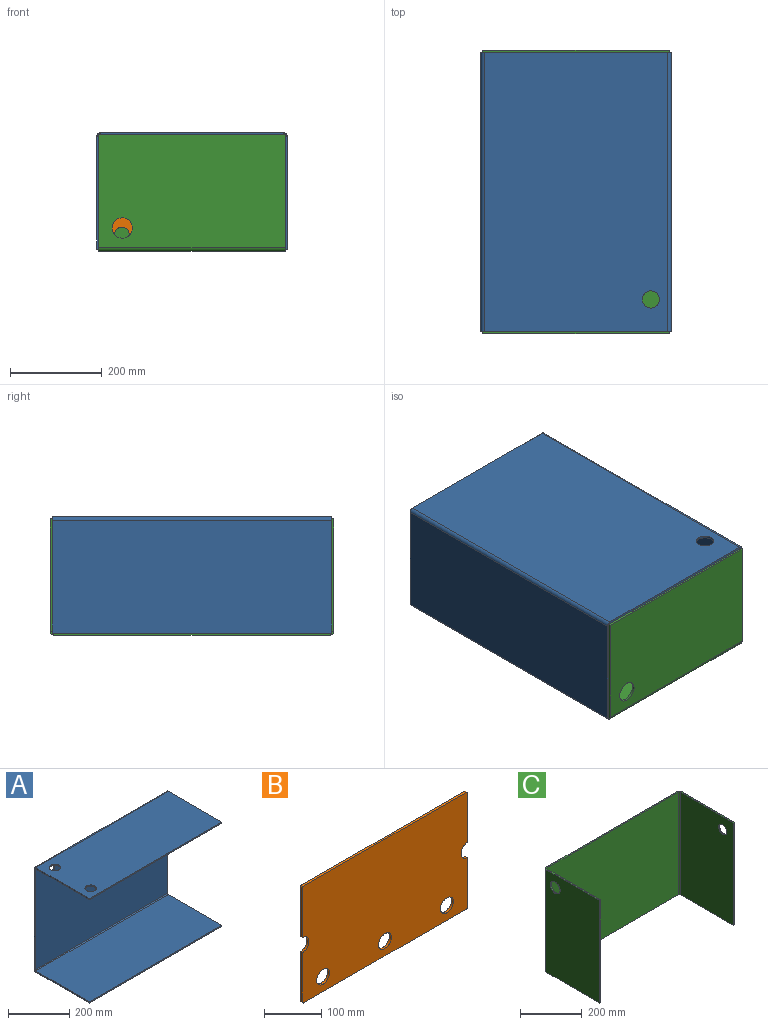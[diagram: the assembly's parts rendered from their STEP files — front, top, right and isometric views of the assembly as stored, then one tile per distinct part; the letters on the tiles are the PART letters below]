
ASSEMBLY  parts=3 mates=2
PART A: 25 faces, bbox 609.6x254x416 mm
  f0: plane 400.05x4.78mm, normal (-1,0,0), area 1910.3mm2, adj f3,f4,f13,f22
  f1: cylinder r=18.73mm len=37.47mm, axis (0,-1,0), area 562mm2, adj f3,f4
  f2: plane 400.05x4.78mm, normal (1,0,0), area 1910.3mm2, adj f3,f4,f12,f21
  f3: plane 609.6x400.05mm, normal (0,1,0), area 242768.1mm2, adj f0,f1,f2,f14,f23
  f4: plane 609.6x400.05mm, normal (0,-1,0), area 242768.1mm2, adj f0,f1,f2,f15,f24
  f5: plane 609.6x4.78mm, normal (0,-1,0), area 2911mm2, adj f6,f9,f10,f11
  f6: plane 246.05x4.78mm, normal (1,0,0), area 1174.9mm2, adj f5,f10,f11,f12
  f7: cylinder r=18.73mm len=37.47mm, axis (0,0,1), area 562mm2, adj f10,f11
  f8: cylinder r=18.73mm len=37.47mm, axis (0,0,1), area 562mm2, adj f10,f11
  f9: plane 246.05x4.78mm, normal (-1,0,0), area 1174.9mm2, adj f5,f10,f11,f13
  f10: plane 609.6x246.05mm, normal (0,0,1), area 147787.1mm2, adj f5,f6,f7,f8,f9,f14
  f11: plane 609.6x246.05mm, normal (0,0,-1), area 147787.1mm2, adj f5,f6,f7,f8,f9,f15
  f12: plane 7.95x7.95mm, normal (1,0,0), area 41.7mm2, adj f2,f6,f14,f15
  f13: plane 7.95x7.95mm, normal (-1,0,0), area 41.7mm2, adj f0,f9,f14,f15
  f14: cylinder r=7.95mm len=609.6mm, axis (1,0,0), area 7612.8mm2, adj f3,f10,f12,f13
  f15: cylinder r=3.17mm len=609.6mm, axis (1,0,0), area 3040.2mm2, adj f4,f11,f12,f13
  f16: plane 609.6x4.78mm, normal (0,-1,0), area 2911mm2, adj f17,f18,f19,f20
  f17: plane 246.05x4.78mm, normal (-1,0,0), area 1174.9mm2, adj f16,f19,f20,f22
  f18: plane 246.05x4.78mm, normal (1,0,0), area 1174.9mm2, adj f16,f19,f20,f21
  f19: plane 609.6x246.05mm, normal (0,0,-1), area 149992mm2, adj f16,f17,f18,f23
  f20: plane 609.6x246.05mm, normal (0,0,1), area 149992mm2, adj f16,f17,f18,f24
  f21: plane 7.95x7.95mm, normal (1,0,0), area 41.7mm2, adj f2,f18,f23,f24
  f22: plane 7.95x7.95mm, normal (-1,0,0), area 41.7mm2, adj f0,f17,f23,f24
  f23: cylinder r=7.95mm len=609.6mm, axis (1,0,0), area 7612.8mm2, adj f3,f19,f21,f22
  f24: cylinder r=3.17mm len=609.6mm, axis (1,0,0), area 3040.2mm2, adj f4,f20,f21,f22
PART B: 17 faces, bbox 406.4x4.8x248.9 mm
  f0: plane 400.05x4.78mm, normal (0,0,1), area 1910.3mm2, adj f1,f13,f15,f16
  f1: cylinder r=3.17mm len=4.78mm, axis (0,1,0), area 23.8mm2, adj f0,f2,f15,f16
  f2: plane 105.41x4.78mm, normal (-1,0,0), area 503.4mm2, adj f1,f3,f15,f16
  f3: cylinder r=15.88mm len=31.75mm, axis (0,1,0), area 238.2mm2, adj f2,f4,f15,f16
  f4: plane 105.41x4.78mm, normal (-1,0,0), area 503.4mm2, adj f3,f5,f15,f16
  f5: cylinder r=3.17mm len=4.78mm, axis (0,1,0), area 23.8mm2, adj f4,f6,f15,f16
  f6: plane 400.05x4.78mm, normal (0,0,-1), area 1910.3mm2, adj f5,f7,f15,f16
  f7: cylinder r=3.17mm len=4.78mm, axis (0,1,0), area 23.8mm2, adj f6,f8,f15,f16
  f8: plane 105.41x4.78mm, normal (1,0,0), area 503.4mm2, adj f7,f9,f15,f16
  f9: cylinder r=15.88mm len=31.75mm, axis (0,1,0), area 238.2mm2, adj f8,f10,f15,f16
  f10: plane 105.41x4.78mm, normal (1,0,0), area 503.4mm2, adj f9,f13,f15,f16
  f11: cylinder r=15.88mm len=31.75mm, axis (0,1,0), area 476.3mm2, adj f15,f16
  f12: cylinder r=15.88mm len=31.75mm, axis (0,1,0), area 476.3mm2, adj f15,f16
  f13: cylinder r=3.17mm len=4.78mm, axis (0,1,0), area 23.8mm2, adj f0,f10,f15,f16
  f14: cylinder r=15.88mm len=31.75mm, axis (0,1,0), area 476.3mm2, adj f15,f16
  f15: plane 406.4x248.92mm, normal (0,-1,0), area 97985.5mm2, adj f0,f1,f2,f3,f4,f5,f6,f7
  f16: plane 406.4x248.92mm, normal (0,1,0), area 97985.5mm2, adj f0,f1,f2,f3,f4,f5,f6,f7
PART C: 24 faces, bbox 619.2x254x406.4 mm
  f0: plane 603.25x4.78mm, normal (0,0,-1), area 2880.6mm2, adj f2,f3,f10,f20
  f1: plane 603.25x4.78mm, normal (0,0,1), area 2880.6mm2, adj f2,f3,f11,f21
  f2: plane 603.25x406.4mm, normal (0,1,0), area 245160.8mm2, adj f0,f1,f12,f22
  f3: plane 603.25x406.4mm, normal (0,-1,0), area 245160.8mm2, adj f0,f1,f13,f23
  f4: plane 406.4x4.78mm, normal (0,-1,0), area 1940.6mm2, adj f5,f7,f8,f9
  f5: plane 246.05x4.78mm, normal (0,0,1), area 1174.9mm2, adj f4,f8,f9,f11
  f6: cylinder r=22.23mm len=44.45mm, axis (-1,0,0), area 666.8mm2, adj f8,f9
  f7: plane 246.05x4.78mm, normal (0,0,-1), area 1174.9mm2, adj f4,f8,f9,f10
  f8: plane 406.4x246.05mm, normal (-1,0,0), area 98442.8mm2, adj f4,f5,f6,f7,f12
  f9: plane 406.4x246.05mm, normal (1,0,0), area 98442.8mm2, adj f4,f5,f6,f7,f13
  f10: plane 7.95x7.95mm, normal (0,0,-1), area 41.7mm2, adj f0,f7,f12,f13
  f11: plane 7.95x7.95mm, normal (0,0,1), area 41.7mm2, adj f1,f5,f12,f13
  f12: cylinder r=7.95mm len=406.4mm, axis (0,0,-1), area 5075.2mm2, adj f2,f8,f10,f11
  f13: cylinder r=3.17mm len=406.4mm, axis (0,0,-1), area 2026.8mm2, adj f3,f9,f10,f11
  f14: plane 406.4x4.78mm, normal (0,-1,0), area 1940.6mm2, adj f15,f17,f18,f19
  f15: plane 246.05x4.78mm, normal (0,0,-1), area 1174.9mm2, adj f14,f18,f19,f20
  f16: cylinder r=18.73mm len=37.47mm, axis (1,0,0), area 562mm2, adj f18,f19
  f17: plane 246.05x4.78mm, normal (0,0,1), area 1174.9mm2, adj f14,f18,f19,f21
  f18: plane 406.4x246.05mm, normal (1,0,0), area 98892.2mm2, adj f14,f15,f16,f17,f22
  f19: plane 406.4x246.05mm, normal (-1,0,0), area 98892.2mm2, adj f14,f15,f16,f17,f23
  f20: plane 7.95x7.95mm, normal (0,0,-1), area 41.7mm2, adj f0,f15,f22,f23
  f21: plane 7.95x7.95mm, normal (0,0,1), area 41.7mm2, adj f1,f17,f22,f23
  f22: cylinder r=7.95mm len=406.4mm, axis (0,0,-1), area 5075.2mm2, adj f2,f18,f20,f21
  f23: cylinder r=3.17mm len=406.4mm, axis (0,0,-1), area 2026.8mm2, adj f3,f19,f20,f21
PLACE A rot(axis=(0.58,0.58,0.58),120deg) t=(-843.41,258.61,108.78)mm
PLACE B t=(-844.15,262.06,-20.46)mm
PLACE C rot(axis=(-0.58,-0.58,0.58),120deg) t=(-843.41,258.61,-150)mm
MATE fastened A.f4 <-> B.f0  axis (0,0,-1) through (-844.15,259.68,104)mm
MATE fastened A.f4 <-> C.f4  axis (0,0,-1) through (-843.41,-46.19,104)mm
